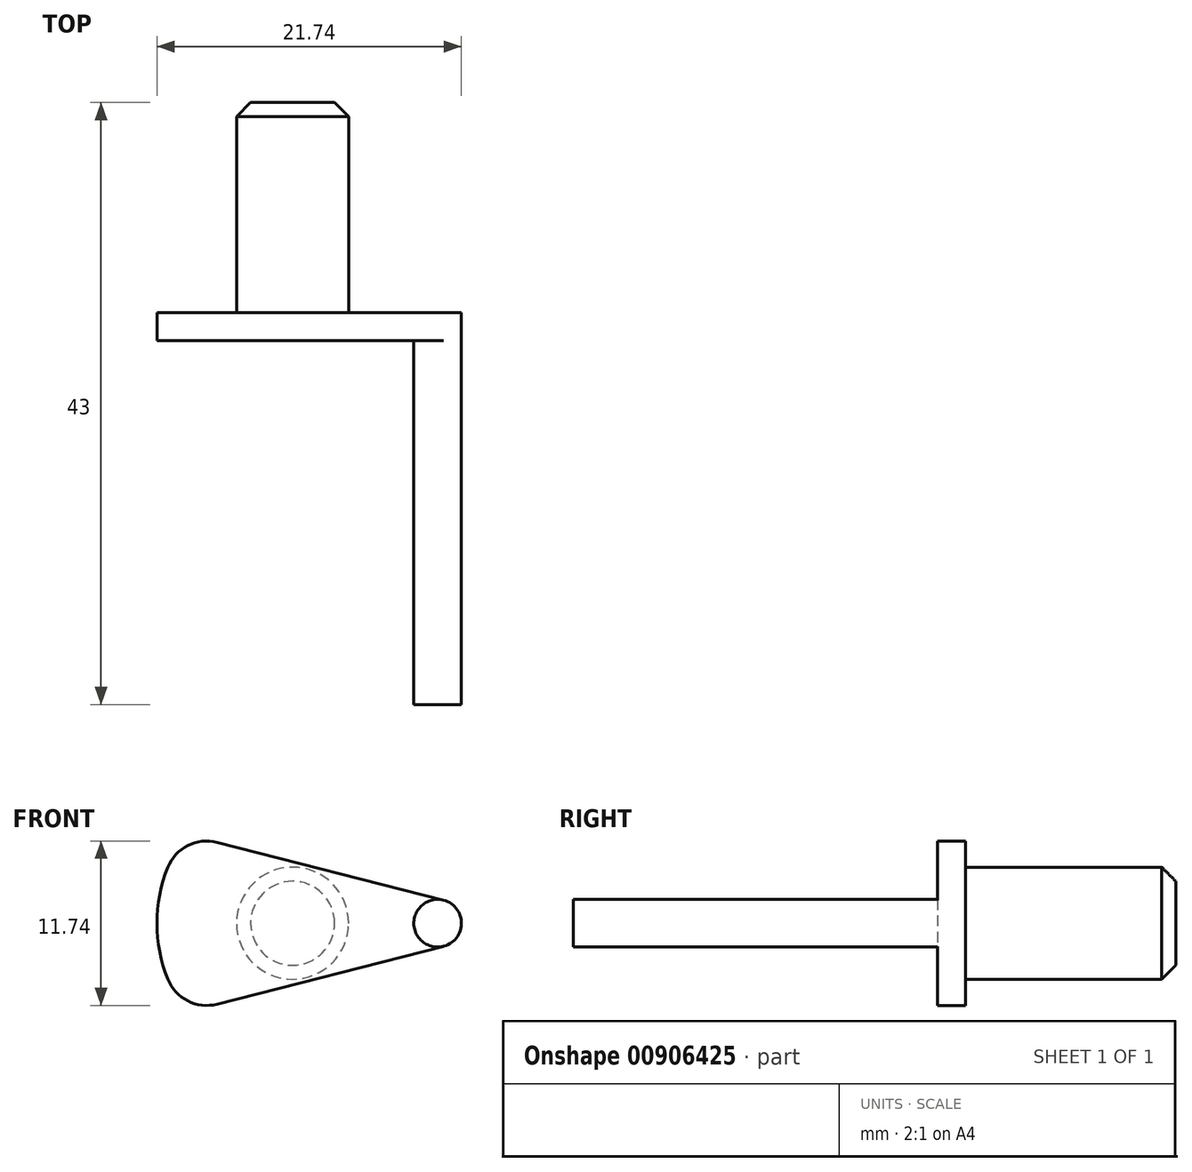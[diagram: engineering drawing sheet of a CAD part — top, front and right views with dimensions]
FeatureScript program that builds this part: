
annotation { "Feature Type Name" : "Feature", "Feature Type Description" : "" }
export const myFeature = defineFeature(function(context is Context, id is Id, definition is map)
    precondition{}
    {
        {
            var Q0;
            Q0=qCreatedBy(makeId("Front.planeOp"),FACE);
            var sketch = newSketch(context, id + "F0", { "sketchPlane" : qUnion([Q0])});
            skLineSegment(sketch, "E0", {"start": v(-10.85, 0) * mm, "end": v(12.06, 0) * mm, "construction": true});
            skArc(sketch, "E1", {"start": v(12.06, 0) * mm, "mid": v(11.7, 1.04) * mm, "end": v(10.78, 1.65) * mm});
            skArc(sketch, "E2", {"start": v(-8.91, 3.99) * mm, "mid": v(-9.48, 2.03) * mm, "end": v(-9.68, 0) * mm});
            skLineSegment(sketch, "E3", {"start": v(10.95, 1.6) * mm, "end": v(-5.38, 5.78) * mm});
            skPoint(sketch, "E4.visualSharp", {"position": v(-7.6, 6.35) * mm});
            skArc(sketch, "E4.filletArc", {"start": v(-5.38, 5.78) * mm, "mid": v(-7.48, 5.55) * mm, "end": v(-8.91, 3.99) * mm});
            skLineSegment(sketch, "E5.MirrorCS", {"start": v(10.95, -1.6) * mm, "end": v(-5.38, -5.78) * mm});
            skArc(sketch, "E6.MirrorCS", {"start": v(-5.38, -5.78) * mm, "mid": v(-7.48, -5.55) * mm, "end": v(-8.91, -3.99) * mm});
            skArc(sketch, "E7.MirrorCS", {"start": v(-8.91, -3.99) * mm, "mid": v(-9.48, -2.03) * mm, "end": v(-9.68, 0) * mm});
            skArc(sketch, "E8.MirrorCS", {"start": v(12.06, 0) * mm, "mid": v(11.7, -1.04) * mm, "end": v(10.78, -1.65) * mm});
            skSolve(sketch);
        }
        {
            var Q0;
            Q0=qSketchRegion(id+"F0",true);
            extrude(context, id + "F1", {"entities" : qUnion([Q0]), "depth" : 2 * mm, "offsetDistance" : 25 * mm});
        }
        {
            var Q0;
            Q0=makeQuery(id+"F1.opExtrude","CAP_FACE",FACE,{"disambiguationData":[OSD([sQuery(id+"F0.wireOp",EDGE,"E1"),sQuery(id+"F0.wireOp",EDGE,"E2"),sQuery(id+"F0.wireOp",EDGE,"E3"),sQuery(id+"F0.wireOp",EDGE,"E4.filletArc"),sQuery(id+"F0.wireOp",EDGE,"E5.MirrorCS"),sQuery(id+"F0.wireOp",EDGE,"E6.MirrorCS"),sQuery(id+"F0.wireOp",EDGE,"E7.MirrorCS"),sQuery(id+"F0.wireOp",EDGE,"E8.MirrorCS")])],"isStart":false});
            var sketch = newSketch(context, id + "F2", { "sketchPlane" : qUnion([Q0])});
            skCircle(sketch, "E9", {"center": v(10.36, 0) * mm, "radius": 1.7 * mm});
            skSolve(sketch);
        }
        {
            var Q0;
            {var subQ0=sQuery(id+"F2.wireOp",EDGE,"E9");Q0=makeQuery(id+"F2.imprint","IMPRINT",FACE,{"disambiguationData":[TD([[makeQuery(id+"F2.imprint","IMPRINT",EDGE,{"disambiguationData":[OD(0.0)],"derivedFrom":subQ0}),1.0]])]});}
            extrude(context, id + "F3", {"entities" : qUnion([Q0]), "operationType" : NewBodyOperationType.ADD, "depth" : 26 * mm, "offsetDistance" : 25 * mm});
        }
        {
            var Q0;
            Q0=makeQuery(id+"F1.opExtrude","CAP_FACE",FACE,{"disambiguationData":[OSD([sQuery(id+"F0.wireOp",EDGE,"E1"),sQuery(id+"F0.wireOp",EDGE,"E2"),sQuery(id+"F0.wireOp",EDGE,"E3"),sQuery(id+"F0.wireOp",EDGE,"E4.filletArc"),sQuery(id+"F0.wireOp",EDGE,"E5.MirrorCS"),sQuery(id+"F0.wireOp",EDGE,"E6.MirrorCS"),sQuery(id+"F0.wireOp",EDGE,"E7.MirrorCS"),sQuery(id+"F0.wireOp",EDGE,"E8.MirrorCS")])],"isStart":true});
            var sketch = newSketch(context, id + "F4", { "sketchPlane" : qUnion([Q0])});
            skCircle(sketch, "E10", {"center": v(0, 0) * mm, "radius": 4 * mm});
            skSolve(sketch);
        }
        {
            var Q0;
            Q0=qSketchRegion(id+"F4",true);
            extrude(context, id + "F5", {"entities" : qUnion([Q0]), "operationType" : NewBodyOperationType.ADD, "depth" : 15 * mm, "offsetDistance" : 25 * mm});
        }
        {
            var Q0;
            Q0=makeQuery(id+"F5.opExtrude","CAP_EDGE",EDGE,{"disambiguationData":[OSD([sQuery(id+"F4.wireOp",EDGE,"E10")])],"isStart":false});
            chamfer(context, id + "F6", {"entities" : qUnion([Q0]), "width" : 1 * mm, "tangentPropagation" : true});
        }
    });
